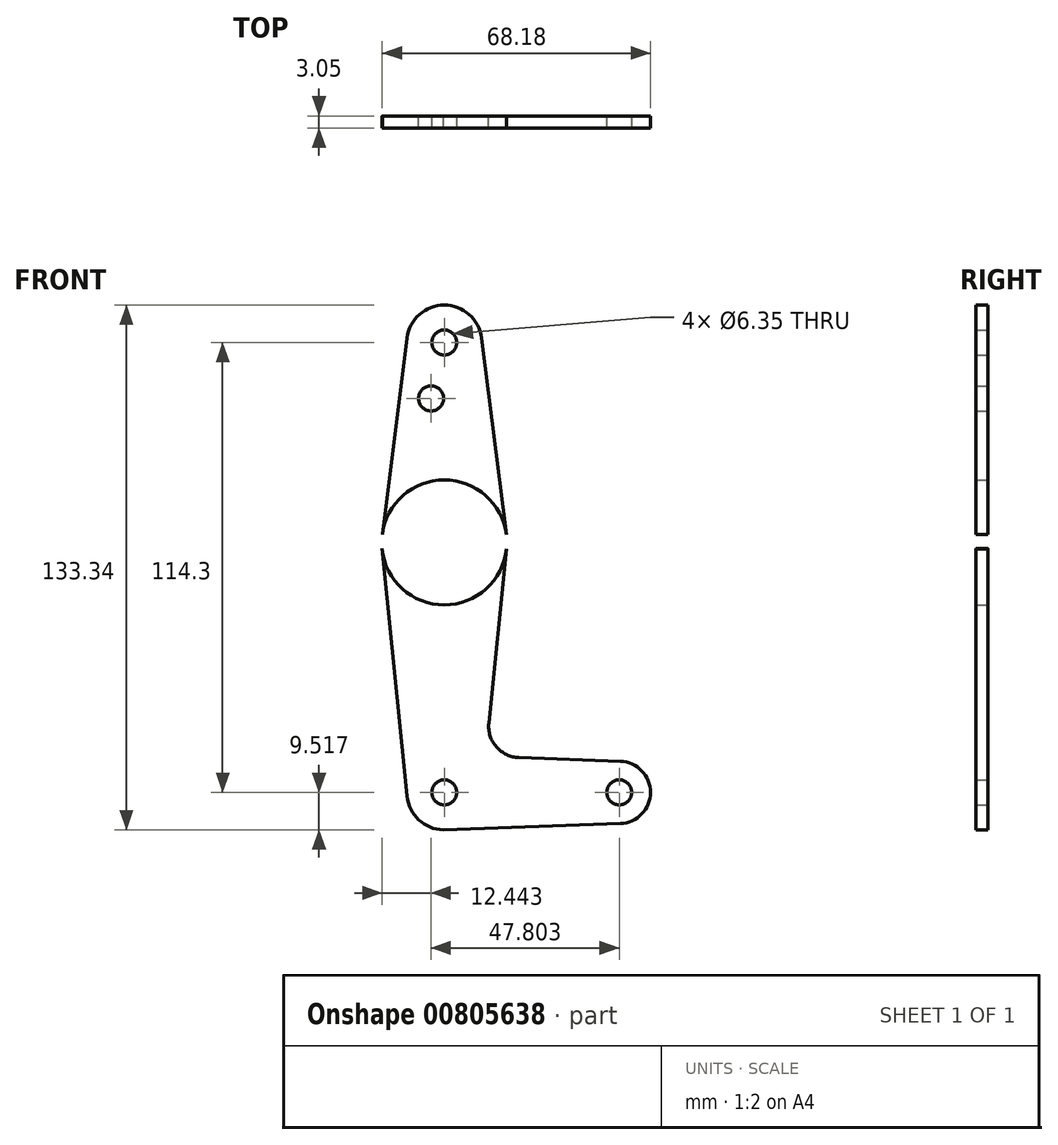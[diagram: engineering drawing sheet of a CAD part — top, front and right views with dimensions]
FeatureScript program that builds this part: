
annotation { "Feature Type Name" : "Feature", "Feature Type Description" : "" }
export const myFeature = defineFeature(function(context is Context, id is Id, definition is map)
    precondition{}
    {
        {
            var Q0;
            Q0=qCreatedBy(makeId("Front.planeOp"),FACE);
            var sketch = newSketch(context, id + "F0", { "sketchPlane" : qUnion([Q0])});
            skLineSegment(sketch, "E0", {"start": v(-24.05, 77.7) * mm, "end": v(-24.05, -36.6) * mm});
            skLineSegment(sketch, "E1", {"start": v(-24.05, -36.6) * mm, "end": v(20.4, -36.6) * mm});
            skCircle(sketch, "E2", {"center": v(-24.05, 77.7) * mm, "radius": 9.53 * mm});
            skCircle(sketch, "E3", {"center": v(-24.05, 26.9) * mm, "radius": 15.88 * mm});
            skCircle(sketch, "E4", {"center": v(-24.05, -36.6) * mm, "radius": 9.53 * mm});
            skCircle(sketch, "E5", {"center": v(20.4, -36.6) * mm, "radius": 7.94 * mm});
            skLineSegment(sketch, "E6", {"start": v(-39.8, 28.9) * mm, "end": v(-33.5, 78.9) * mm});
            skLineSegment(sketch, "E7", {"start": v(-8.3, 28.9) * mm, "end": v(-14.6, 78.9) * mm});
            skLineSegment(sketch, "E8", {"start": v(-24.3, -46.11) * mm, "end": v(20.68, -44.53) * mm});
            skLineSegment(sketch, "E9", {"start": v(-5.12, -27.74) * mm, "end": v(20.68, -28.66) * mm});
            skLineSegment(sketch, "E10", {"start": v(-39.85, 25.32) * mm, "end": v(-33.53, -37.55) * mm});
            skLineSegment(sketch, "E11", {"start": v(-12.75, -19) * mm, "end": v(-8.26, 25.3) * mm});
            skCircle(sketch, "E12", {"center": v(-24.05, 77.7) * mm, "radius": 3.18 * mm});
            skCircle(sketch, "E13", {"center": v(-24.05, 26.9) * mm, "radius": 3.18 * mm});
            skCircle(sketch, "E14", {"center": v(-24.05, -36.6) * mm, "radius": 3.18 * mm});
            skCircle(sketch, "E15", {"center": v(20.4, -36.6) * mm, "radius": 3.18 * mm});
            skCircle(sketch, "E16", {"center": v(-27.4, 63.51) * mm, "radius": 3.18 * mm});
            skArc(sketch, "E17.filletArc", {"start": v(-12.75, -19) * mm, "mid": v(-10.83, -25.02) * mm, "end": v(-5.12, -27.74) * mm});
            skSolve(sketch);
        }
        {
            var Q0;
            {var subQ5=sQuery(id+"F0.wireOp",EDGE,"E10");Q0=makeQuery(id+"F0.imprint","IMPRINT",FACE,{"disambiguationData":[TD([[makeQuery(id+"F0.imprint","IMPRINT",EDGE,{"derivedFrom":subQ5}),1.0]])]});}
            var Q1;
            {var subQ1=sQuery(id+"F0.wireOp",EDGE,"E4");var subQ8=sQuery(id+"F0.wireOp",EDGE,"E0");var subQ9=makeQuery(id+"F0.imprint","INTERSECT",VERTEX,{"derivedFrom":[subQ8,subQ1]});Q1=makeQuery(id+"F0.imprint","IMPRINT",FACE,{"disambiguationData":[TD([[makeQuery(id+"F0.imprint","IMPRINT",EDGE,{"disambiguationData":[TD([[subQ9,-1.0]])],"derivedFrom":subQ8}),-1.0]])]});}
            var Q2;
            {var subQ0=sQuery(id+"F0.wireOp",EDGE,"E4");var subQ1=sQuery(id+"F0.wireOp",EDGE,"E0");var subQ2=makeQuery(id+"F0.imprint","INTERSECT",VERTEX,{"derivedFrom":[subQ1,subQ0]});Q2=makeQuery(id+"F0.imprint","IMPRINT",FACE,{"disambiguationData":[TD([[makeQuery(id+"F0.imprint","IMPRINT",EDGE,{"disambiguationData":[TD([[subQ2,-1.0]])],"derivedFrom":subQ1}),1.0]])]});}
            var Q3;
            {var subQ0=sQuery(id+"F0.wireOp",EDGE,"E5");var subQ1=sQuery(id+"F0.wireOp",EDGE,"E1");var subQ2=makeQuery(id+"F0.imprint","INTERSECT",VERTEX,{"derivedFrom":[subQ1,subQ0]});Q3=makeQuery(id+"F0.imprint","IMPRINT",FACE,{"disambiguationData":[TD([[makeQuery(id+"F0.imprint","IMPRINT",EDGE,{"disambiguationData":[TD([[subQ2,1.0]])],"derivedFrom":subQ1}),-1.0]])]});}
            var Q4;
            {var subQ10=sQuery(id+"F0.wireOp",EDGE,"E9");Q4=makeQuery(id+"F0.imprint","IMPRINT",FACE,{"disambiguationData":[TD([[makeQuery(id+"F0.imprint","IMPRINT",EDGE,{"derivedFrom":subQ10}),-1.0]])]});}
            var Q5;
            Q5=makeQuery(id+"F0.imprint","IMPRINT",FACE,{"disambiguationData":[TD([[makeQuery(id+"F0.imprint","IMPRINT",EDGE,{"derivedFrom":sQuery(id+"F0.wireOp",EDGE,"E15")}),-1.0]])]});
            var Q6;
            {var subQ0=sQuery(id+"F0.wireOp",EDGE,"E3");var subQ2=sQuery(id+"F0.wireOp",EDGE,"E0");var subQ5=makeQuery(id+"F0.imprint","INTERSECT",VERTEX,{"disambiguationData":[OD(0.0)],"derivedFrom":[subQ2,subQ0]});Q6=makeQuery(id+"F0.imprint","IMPRINT",FACE,{"disambiguationData":[TD([[makeQuery(id+"F0.imprint","IMPRINT",EDGE,{"disambiguationData":[TD([[subQ5,-1.0]])],"derivedFrom":subQ2}),1.0]])]});}
            var Q7;
            {var subQ0=sQuery(id+"F0.wireOp",EDGE,"E3");var subQ3=sQuery(id+"F0.wireOp",EDGE,"E0");var subQ4=makeQuery(id+"F0.imprint","INTERSECT",VERTEX,{"disambiguationData":[OD(0.0)],"derivedFrom":[subQ3,subQ0]});Q7=makeQuery(id+"F0.imprint","IMPRINT",FACE,{"disambiguationData":[TD([[makeQuery(id+"F0.imprint","IMPRINT",EDGE,{"disambiguationData":[TD([[subQ4,-1.0]])],"derivedFrom":subQ3}),-1.0]])]});}
            var Q8;
            {var subQ0=sQuery(id+"F0.wireOp",EDGE,"E6");Q8=makeQuery(id+"F0.imprint","IMPRINT",FACE,{"disambiguationData":[TD([[makeQuery(id+"F0.imprint","IMPRINT",EDGE,{"derivedFrom":subQ0}),-1.0]])]});}
            var Q9;
            {var subQ5=sQuery(id+"F0.wireOp",EDGE,"E7");Q9=makeQuery(id+"F0.imprint","IMPRINT",FACE,{"disambiguationData":[TD([[makeQuery(id+"F0.imprint","IMPRINT",EDGE,{"derivedFrom":subQ5}),1.0]])]});}
            var Q10;
            Q10=makeQuery(id+"F0.imprint","IMPRINT",FACE,{"disambiguationData":[TD([[makeQuery(id+"F0.imprint","IMPRINT",EDGE,{"derivedFrom":sQuery(id+"F0.wireOp",EDGE,"E12")}),-1.0]])]});
            extrude(context, id + "F1", {"entities" : qUnion([Q0, Q1, Q2, Q3, Q4, Q5, Q6, Q7, Q8, Q9, Q10]), "depth" : 3.05 * mm, "offsetDistance" : 25.4 * mm});
        }
    });
